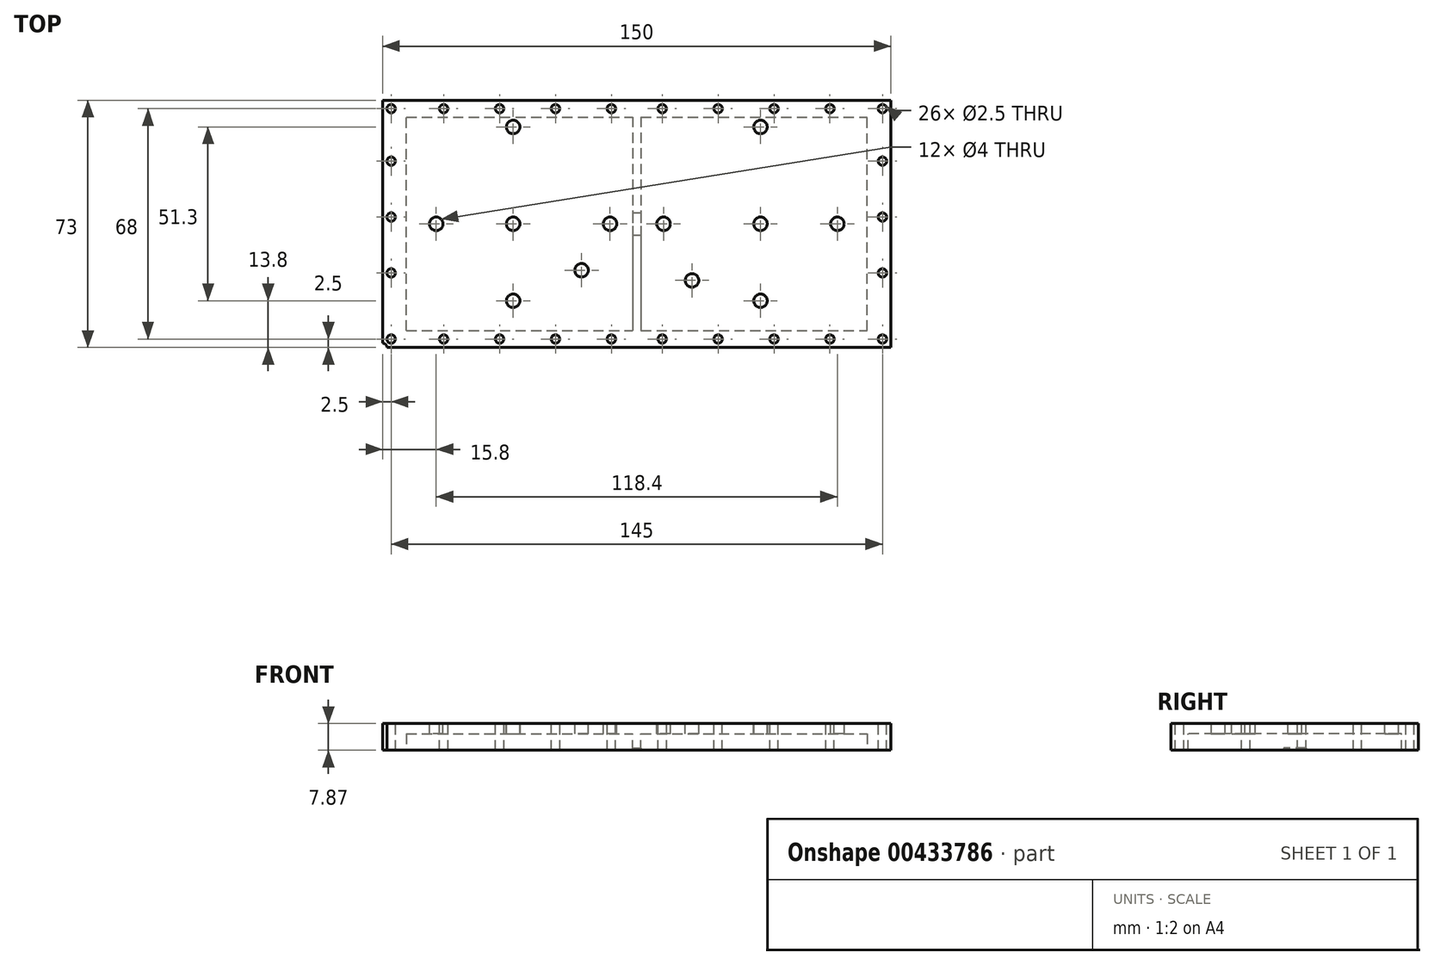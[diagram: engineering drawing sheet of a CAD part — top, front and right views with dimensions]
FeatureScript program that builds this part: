
annotation { "Feature Type Name" : "Feature", "Feature Type Description" : "" }
export const myFeature = defineFeature(function(context is Context, id is Id, definition is map)
    precondition{}
    {
        {
            var Q0;
            Q0=qCreatedBy(makeId("Top.planeOp"),FACE);
            var sketch = newSketch(context, id + "F0", { "sketchPlane" : qUnion([Q0])});
            skLineSegment(sketch, "E0.bottom", {"start": v(0, 0) * mm, "end": v(150, 0) * mm});
            skLineSegment(sketch, "E0.top", {"start": v(0, 73) * mm, "end": v(150, 73) * mm});
            skLineSegment(sketch, "E0.left", {"start": v(0, 0) * mm, "end": v(0, 73) * mm});
            skLineSegment(sketch, "E0.right", {"start": v(150, 0) * mm, "end": v(150, 73) * mm});
            skSolve(sketch);
        }
        {
            var Q0;
            Q0=qSketchRegion(id+"F0",true);
            extrude(context, id + "F1", {"entities" : qUnion([Q0]), "depth" : 7.87 * mm});
        }
        {
            var Q0;
            Q0=qCreatedBy(makeId("Top.planeOp"),FACE);
            var sketch = newSketch(context, id + "F2", { "sketchPlane" : qUnion([Q0])});
            skLineSegment(sketch, "E1.bottom", {"start": v(7, 5) * mm, "end": v(143, 5) * mm});
            skLineSegment(sketch, "E1.top", {"start": v(7, 68) * mm, "end": v(143, 68) * mm});
            skLineSegment(sketch, "E1.left", {"start": v(7, 5) * mm, "end": v(7, 68) * mm});
            skLineSegment(sketch, "E1.right", {"start": v(143, 5) * mm, "end": v(143, 68) * mm});
            skSolve(sketch);
        }
        {
            var Q0;
            Q0=qSketchRegion(id+"F2",true);
            extrude(context, id + "F3", {"entities" : qUnion([Q0]), "operationType" : NewBodyOperationType.REMOVE, "depth" : 4.87 * mm});
        }
        {
            var Q0;
            Q0=makeQuery(id+"F1.opExtrude","CAP_FACE",FACE,{"disambiguationData":[OSD([sQuery(id+"F0.wireOp",EDGE,"E0.bottom"),sQuery(id+"F0.wireOp",EDGE,"E0.top"),sQuery(id+"F0.wireOp",EDGE,"E0.left"),sQuery(id+"F0.wireOp",EDGE,"E0.right")])],"isStart":false});
            var sketch = newSketch(context, id + "F4", { "sketchPlane" : qUnion([Q0])});
            skCircle(sketch, "E2", {"center": v(2.5, 2.5) * mm, "radius": 1.25 * mm});
            skSolve(sketch);
        }
        {
            var Q0;
            Q0=qSketchRegion(id+"F4",true);
            extrude(context, id + "F5", {"entities" : qUnion([Q0]), "operationType" : NewBodyOperationType.REMOVE, "oppositeDirection" : true, "depth" : 7.87 * mm});
        }
        {
            var Q0;
            Q0=makeQuery(id+"F1.opExtrude","CAP_FACE",FACE,{"disambiguationData":[OSD([sQuery(id+"F0.wireOp",EDGE,"E0.bottom"),sQuery(id+"F0.wireOp",EDGE,"E0.top"),sQuery(id+"F0.wireOp",EDGE,"E0.left"),sQuery(id+"F0.wireOp",EDGE,"E0.right")])],"isStart":false});
            var sketch = newSketch(context, id + "F6", { "sketchPlane" : qUnion([Q0])});
            skCircle(sketch, "E3", {"center": v(18, 2.5) * mm, "radius": 1.25 * mm});
            skSolve(sketch);
        }
        {
            var Q0;
            Q0=qSketchRegion(id+"F6",true);
            extrude(context, id + "F7", {"entities" : qUnion([Q0]), "operationType" : NewBodyOperationType.REMOVE, "oppositeDirection" : true, "depth" : 7.87 * mm});
        }
        {
            var Q0;
            Q0=makeQuery(id+"F1.opExtrude","CAP_FACE",FACE,{"disambiguationData":[OSD([sQuery(id+"F0.wireOp",EDGE,"E0.bottom"),sQuery(id+"F0.wireOp",EDGE,"E0.top"),sQuery(id+"F0.wireOp",EDGE,"E0.left"),sQuery(id+"F0.wireOp",EDGE,"E0.right")])],"isStart":false});
            var sketch = newSketch(context, id + "F8", { "sketchPlane" : qUnion([Q0])});
            skCircle(sketch, "E4", {"center": v(34.5, 2.5) * mm, "radius": 1.25 * mm});
            skSolve(sketch);
        }
        {
            var Q0;
            Q0=qSketchRegion(id+"F8",true);
            extrude(context, id + "F9", {"entities" : qUnion([Q0]), "operationType" : NewBodyOperationType.REMOVE, "oppositeDirection" : true, "depth" : 7.87 * mm});
        }
        {
            var Q0;
            Q0=makeQuery(id+"F1.opExtrude","CAP_FACE",FACE,{"disambiguationData":[OSD([sQuery(id+"F0.wireOp",EDGE,"E0.bottom"),sQuery(id+"F0.wireOp",EDGE,"E0.top"),sQuery(id+"F0.wireOp",EDGE,"E0.left"),sQuery(id+"F0.wireOp",EDGE,"E0.right")])],"isStart":false});
            var sketch = newSketch(context, id + "F10", { "sketchPlane" : qUnion([Q0])});
            skCircle(sketch, "E5", {"center": v(51, 2.5) * mm, "radius": 1.25 * mm});
            skSolve(sketch);
        }
        {
            var Q0;
            Q0=qSketchRegion(id+"F10",true);
            extrude(context, id + "F11", {"entities" : qUnion([Q0]), "operationType" : NewBodyOperationType.REMOVE, "oppositeDirection" : true, "depth" : 7.87 * mm});
        }
        {
            var Q0;
            Q0=makeQuery(id+"F1.opExtrude","CAP_FACE",FACE,{"disambiguationData":[OSD([sQuery(id+"F0.wireOp",EDGE,"E0.bottom"),sQuery(id+"F0.wireOp",EDGE,"E0.top"),sQuery(id+"F0.wireOp",EDGE,"E0.left"),sQuery(id+"F0.wireOp",EDGE,"E0.right")])],"isStart":false});
            var sketch = newSketch(context, id + "F12", { "sketchPlane" : qUnion([Q0])});
            skCircle(sketch, "E6", {"center": v(67.5, 2.5) * mm, "radius": 1.25 * mm});
            skSolve(sketch);
        }
        {
            var Q0;
            Q0=qSketchRegion(id+"F12",true);
            extrude(context, id + "F13", {"entities" : qUnion([Q0]), "operationType" : NewBodyOperationType.REMOVE, "oppositeDirection" : true, "depth" : 7.87 * mm});
        }
        {
            var Q0;
            Q0=makeQuery(id+"F1.opExtrude","CAP_FACE",FACE,{"disambiguationData":[OSD([sQuery(id+"F0.wireOp",EDGE,"E0.bottom"),sQuery(id+"F0.wireOp",EDGE,"E0.top"),sQuery(id+"F0.wireOp",EDGE,"E0.left"),sQuery(id+"F0.wireOp",EDGE,"E0.right")])],"isStart":false});
            var sketch = newSketch(context, id + "F14", { "sketchPlane" : qUnion([Q0])});
            skCircle(sketch, "E7", {"center": v(82.5, 2.5) * mm, "radius": 1.25 * mm});
            skSolve(sketch);
        }
        {
            var Q0;
            Q0=qSketchRegion(id+"F14",true);
            extrude(context, id + "F15", {"entities" : qUnion([Q0]), "operationType" : NewBodyOperationType.REMOVE, "oppositeDirection" : true, "depth" : 7.87 * mm});
        }
        {
            var Q0;
            Q0=makeQuery(id+"F1.opExtrude","CAP_FACE",FACE,{"disambiguationData":[OSD([sQuery(id+"F0.wireOp",EDGE,"E0.bottom"),sQuery(id+"F0.wireOp",EDGE,"E0.top"),sQuery(id+"F0.wireOp",EDGE,"E0.left"),sQuery(id+"F0.wireOp",EDGE,"E0.right")])],"isStart":false});
            var sketch = newSketch(context, id + "F16", { "sketchPlane" : qUnion([Q0])});
            skCircle(sketch, "E8", {"center": v(99, 2.5) * mm, "radius": 1.25 * mm});
            skSolve(sketch);
        }
        {
            var Q0;
            Q0=qSketchRegion(id+"F16",true);
            extrude(context, id + "F17", {"entities" : qUnion([Q0]), "operationType" : NewBodyOperationType.REMOVE, "oppositeDirection" : true, "depth" : 7.87 * mm});
        }
        {
            var Q0;
            Q0=makeQuery(id+"F1.opExtrude","CAP_FACE",FACE,{"disambiguationData":[OSD([sQuery(id+"F0.wireOp",EDGE,"E0.bottom"),sQuery(id+"F0.wireOp",EDGE,"E0.top"),sQuery(id+"F0.wireOp",EDGE,"E0.left"),sQuery(id+"F0.wireOp",EDGE,"E0.right")])],"isStart":false});
            var sketch = newSketch(context, id + "F18", { "sketchPlane" : qUnion([Q0])});
            skCircle(sketch, "E9", {"center": v(115.5, 2.5) * mm, "radius": 1.25 * mm});
            skSolve(sketch);
        }
        {
            var Q0;
            Q0=qSketchRegion(id+"F18",true);
            extrude(context, id + "F19", {"entities" : qUnion([Q0]), "operationType" : NewBodyOperationType.REMOVE, "oppositeDirection" : true, "depth" : 7.87 * mm});
        }
        {
            var Q0;
            Q0=makeQuery(id+"F1.opExtrude","CAP_FACE",FACE,{"disambiguationData":[OSD([sQuery(id+"F0.wireOp",EDGE,"E0.bottom"),sQuery(id+"F0.wireOp",EDGE,"E0.top"),sQuery(id+"F0.wireOp",EDGE,"E0.left"),sQuery(id+"F0.wireOp",EDGE,"E0.right")])],"isStart":false});
            var sketch = newSketch(context, id + "F20", { "sketchPlane" : qUnion([Q0])});
            skCircle(sketch, "E10", {"center": v(132, 2.5) * mm, "radius": 1.25 * mm});
            skSolve(sketch);
        }
        {
            var Q0;
            Q0=qSketchRegion(id+"F20",true);
            extrude(context, id + "F21", {"entities" : qUnion([Q0]), "operationType" : NewBodyOperationType.REMOVE, "oppositeDirection" : true, "depth" : 7.87 * mm});
        }
        {
            var Q0;
            Q0=makeQuery(id+"F1.opExtrude","CAP_FACE",FACE,{"disambiguationData":[OSD([sQuery(id+"F0.wireOp",EDGE,"E0.bottom"),sQuery(id+"F0.wireOp",EDGE,"E0.top"),sQuery(id+"F0.wireOp",EDGE,"E0.left"),sQuery(id+"F0.wireOp",EDGE,"E0.right")])],"isStart":false});
            var sketch = newSketch(context, id + "F22", { "sketchPlane" : qUnion([Q0])});
            skCircle(sketch, "E11", {"center": v(147.5, 2.5) * mm, "radius": 1.25 * mm});
            skSolve(sketch);
        }
        {
            var Q0;
            Q0=qSketchRegion(id+"F22",true);
            extrude(context, id + "F23", {"entities" : qUnion([Q0]), "operationType" : NewBodyOperationType.REMOVE, "oppositeDirection" : true, "depth" : 7.87 * mm});
        }
        {
            var Q0;
            Q0=makeQuery(id+"F1.opExtrude","CAP_FACE",FACE,{"disambiguationData":[OSD([sQuery(id+"F0.wireOp",EDGE,"E0.bottom"),sQuery(id+"F0.wireOp",EDGE,"E0.top"),sQuery(id+"F0.wireOp",EDGE,"E0.left"),sQuery(id+"F0.wireOp",EDGE,"E0.right")])],"isStart":false});
            var sketch = newSketch(context, id + "F24", { "sketchPlane" : qUnion([Q0])});
            skCircle(sketch, "E12", {"center": v(2.5, 22) * mm, "radius": 1.25 * mm});
            skSolve(sketch);
        }
        {
            var Q0;
            Q0=qSketchRegion(id+"F24",true);
            extrude(context, id + "F25", {"entities" : qUnion([Q0]), "operationType" : NewBodyOperationType.REMOVE, "oppositeDirection" : true, "depth" : 7.87 * mm});
        }
        {
            var Q0;
            Q0=makeQuery(id+"F1.opExtrude","CAP_FACE",FACE,{"disambiguationData":[OSD([sQuery(id+"F0.wireOp",EDGE,"E0.bottom"),sQuery(id+"F0.wireOp",EDGE,"E0.top"),sQuery(id+"F0.wireOp",EDGE,"E0.left"),sQuery(id+"F0.wireOp",EDGE,"E0.right")])],"isStart":false});
            var sketch = newSketch(context, id + "F26", { "sketchPlane" : qUnion([Q0])});
            skCircle(sketch, "E13", {"center": v(147.5, 22) * mm, "radius": 1.25 * mm});
            skSolve(sketch);
        }
        {
            var Q0;
            Q0=qSketchRegion(id+"F26",true);
            extrude(context, id + "F27", {"entities" : qUnion([Q0]), "operationType" : NewBodyOperationType.REMOVE, "oppositeDirection" : true, "depth" : 7.87 * mm});
        }
        {
            var Q0;
            Q0=makeQuery(id+"F1.opExtrude","CAP_FACE",FACE,{"disambiguationData":[OSD([sQuery(id+"F0.wireOp",EDGE,"E0.bottom"),sQuery(id+"F0.wireOp",EDGE,"E0.top"),sQuery(id+"F0.wireOp",EDGE,"E0.left"),sQuery(id+"F0.wireOp",EDGE,"E0.right")])],"isStart":false});
            var sketch = newSketch(context, id + "F28", { "sketchPlane" : qUnion([Q0])});
            skCircle(sketch, "E14", {"center": v(147.5, 38.5) * mm, "radius": 1.25 * mm});
            skSolve(sketch);
        }
        {
            var Q0;
            Q0=qSketchRegion(id+"F28",true);
            extrude(context, id + "F29", {"entities" : qUnion([Q0]), "operationType" : NewBodyOperationType.REMOVE, "oppositeDirection" : true, "depth" : 7.87 * mm});
        }
        {
            var Q0;
            Q0=makeQuery(id+"F1.opExtrude","CAP_FACE",FACE,{"disambiguationData":[OSD([sQuery(id+"F0.wireOp",EDGE,"E0.bottom"),sQuery(id+"F0.wireOp",EDGE,"E0.top"),sQuery(id+"F0.wireOp",EDGE,"E0.left"),sQuery(id+"F0.wireOp",EDGE,"E0.right")])],"isStart":false});
            var sketch = newSketch(context, id + "F30", { "sketchPlane" : qUnion([Q0])});
            skCircle(sketch, "E15", {"center": v(2.5, 38.5) * mm, "radius": 1.25 * mm});
            skSolve(sketch);
        }
        {
            var Q0;
            Q0=qSketchRegion(id+"F30",true);
            extrude(context, id + "F31", {"entities" : qUnion([Q0]), "operationType" : NewBodyOperationType.REMOVE, "oppositeDirection" : true, "depth" : 7.87 * mm});
        }
        {
            var Q0;
            Q0=makeQuery(id+"F1.opExtrude","CAP_FACE",FACE,{"disambiguationData":[OSD([sQuery(id+"F0.wireOp",EDGE,"E0.bottom"),sQuery(id+"F0.wireOp",EDGE,"E0.top"),sQuery(id+"F0.wireOp",EDGE,"E0.left"),sQuery(id+"F0.wireOp",EDGE,"E0.right")])],"isStart":false});
            var sketch = newSketch(context, id + "F32", { "sketchPlane" : qUnion([Q0])});
            skCircle(sketch, "E16", {"center": v(2.5, 55) * mm, "radius": 1.25 * mm});
            skSolve(sketch);
        }
        {
            var Q0;
            Q0=qSketchRegion(id+"F32",true);
            extrude(context, id + "F33", {"entities" : qUnion([Q0]), "operationType" : NewBodyOperationType.REMOVE, "oppositeDirection" : true, "depth" : 7.87 * mm});
        }
        {
            var Q0;
            Q0=makeQuery(id+"F1.opExtrude","CAP_FACE",FACE,{"disambiguationData":[OSD([sQuery(id+"F0.wireOp",EDGE,"E0.bottom"),sQuery(id+"F0.wireOp",EDGE,"E0.top"),sQuery(id+"F0.wireOp",EDGE,"E0.left"),sQuery(id+"F0.wireOp",EDGE,"E0.right")])],"isStart":false});
            var sketch = newSketch(context, id + "F34", { "sketchPlane" : qUnion([Q0])});
            skCircle(sketch, "E17", {"center": v(147.5, 55) * mm, "radius": 1.25 * mm});
            skSolve(sketch);
        }
        {
            var Q0;
            Q0=qSketchRegion(id+"F34",true);
            extrude(context, id + "F35", {"entities" : qUnion([Q0]), "operationType" : NewBodyOperationType.REMOVE, "oppositeDirection" : true, "depth" : 7.87 * mm});
        }
        {
            var Q0;
            Q0=makeQuery(id+"F1.opExtrude","CAP_FACE",FACE,{"disambiguationData":[OSD([sQuery(id+"F0.wireOp",EDGE,"E0.bottom"),sQuery(id+"F0.wireOp",EDGE,"E0.top"),sQuery(id+"F0.wireOp",EDGE,"E0.left"),sQuery(id+"F0.wireOp",EDGE,"E0.right")])],"isStart":false});
            var sketch = newSketch(context, id + "F36", { "sketchPlane" : qUnion([Q0])});
            skCircle(sketch, "E18", {"center": v(2.5, 70.5) * mm, "radius": 1.25 * mm});
            skSolve(sketch);
        }
        {
            var Q0;
            Q0=qSketchRegion(id+"F36",true);
            extrude(context, id + "F37", {"entities" : qUnion([Q0]), "operationType" : NewBodyOperationType.REMOVE, "oppositeDirection" : true, "depth" : 7.87 * mm});
        }
        {
            var Q0;
            Q0=makeQuery(id+"F1.opExtrude","CAP_FACE",FACE,{"disambiguationData":[OSD([sQuery(id+"F0.wireOp",EDGE,"E0.bottom"),sQuery(id+"F0.wireOp",EDGE,"E0.top"),sQuery(id+"F0.wireOp",EDGE,"E0.left"),sQuery(id+"F0.wireOp",EDGE,"E0.right")])],"isStart":false});
            var sketch = newSketch(context, id + "F38", { "sketchPlane" : qUnion([Q0])});
            skCircle(sketch, "E19", {"center": v(147.5, 70.5) * mm, "radius": 1.25 * mm});
            skSolve(sketch);
        }
        {
            var Q0;
            Q0=qSketchRegion(id+"F38",true);
            extrude(context, id + "F39", {"entities" : qUnion([Q0]), "operationType" : NewBodyOperationType.REMOVE, "oppositeDirection" : true, "depth" : 7.87 * mm});
        }
        {
            var Q0;
            Q0=makeQuery(id+"F1.opExtrude","CAP_FACE",FACE,{"disambiguationData":[OSD([sQuery(id+"F0.wireOp",EDGE,"E0.bottom"),sQuery(id+"F0.wireOp",EDGE,"E0.top"),sQuery(id+"F0.wireOp",EDGE,"E0.left"),sQuery(id+"F0.wireOp",EDGE,"E0.right")])],"isStart":false});
            var sketch = newSketch(context, id + "F40", { "sketchPlane" : qUnion([Q0])});
            skCircle(sketch, "E20", {"center": v(18, 70.5) * mm, "radius": 1.25 * mm});
            skSolve(sketch);
        }
        {
            var Q0;
            Q0=qSketchRegion(id+"F40",true);
            extrude(context, id + "F41", {"entities" : qUnion([Q0]), "operationType" : NewBodyOperationType.REMOVE, "oppositeDirection" : true, "depth" : 7.87 * mm});
        }
        {
            var Q0;
            Q0=makeQuery(id+"F1.opExtrude","CAP_FACE",FACE,{"disambiguationData":[OSD([sQuery(id+"F0.wireOp",EDGE,"E0.bottom"),sQuery(id+"F0.wireOp",EDGE,"E0.top"),sQuery(id+"F0.wireOp",EDGE,"E0.left"),sQuery(id+"F0.wireOp",EDGE,"E0.right")])],"isStart":false});
            var sketch = newSketch(context, id + "F42", { "sketchPlane" : qUnion([Q0])});
            skCircle(sketch, "E21", {"center": v(132, 70.5) * mm, "radius": 1.25 * mm});
            skSolve(sketch);
        }
        {
            var Q0;
            Q0=qSketchRegion(id+"F42",true);
            extrude(context, id + "F43", {"entities" : qUnion([Q0]), "operationType" : NewBodyOperationType.REMOVE, "oppositeDirection" : true, "depth" : 7.87 * mm});
        }
        {
            var Q0;
            Q0=makeQuery(id+"F1.opExtrude","CAP_FACE",FACE,{"disambiguationData":[OSD([sQuery(id+"F0.wireOp",EDGE,"E0.bottom"),sQuery(id+"F0.wireOp",EDGE,"E0.top"),sQuery(id+"F0.wireOp",EDGE,"E0.left"),sQuery(id+"F0.wireOp",EDGE,"E0.right")])],"isStart":false});
            var sketch = newSketch(context, id + "F44", { "sketchPlane" : qUnion([Q0])});
            skCircle(sketch, "E22", {"center": v(34.5, 70.5) * mm, "radius": 1.25 * mm});
            skCircle(sketch, "E23", {"center": v(0, 0) * mm, "radius": 1.25 * mm});
            skSolve(sketch);
        }
        {
            var Q0;
            Q0=qSketchRegion(id+"F44",true);
            extrude(context, id + "F45", {"entities" : qUnion([Q0]), "operationType" : NewBodyOperationType.REMOVE, "oppositeDirection" : true, "depth" : 7.87 * mm});
        }
        {
            var Q0;
            Q0=makeQuery(id+"F1.opExtrude","CAP_FACE",FACE,{"disambiguationData":[OSD([sQuery(id+"F0.wireOp",EDGE,"E0.bottom"),sQuery(id+"F0.wireOp",EDGE,"E0.top"),sQuery(id+"F0.wireOp",EDGE,"E0.left"),sQuery(id+"F0.wireOp",EDGE,"E0.right")])],"isStart":false});
            var sketch = newSketch(context, id + "F46", { "sketchPlane" : qUnion([Q0])});
            skCircle(sketch, "E24", {"center": v(115.5, 70.5) * mm, "radius": 1.25 * mm});
            skSolve(sketch);
        }
        {
            var Q0;
            Q0=qSketchRegion(id+"F46",true);
            extrude(context, id + "F47", {"entities" : qUnion([Q0]), "operationType" : NewBodyOperationType.REMOVE, "oppositeDirection" : true, "depth" : 7.87 * mm});
        }
        {
            var Q0;
            Q0=makeQuery(id+"F1.opExtrude","CAP_FACE",FACE,{"disambiguationData":[OSD([sQuery(id+"F0.wireOp",EDGE,"E0.bottom"),sQuery(id+"F0.wireOp",EDGE,"E0.top"),sQuery(id+"F0.wireOp",EDGE,"E0.left"),sQuery(id+"F0.wireOp",EDGE,"E0.right")])],"isStart":false});
            var sketch = newSketch(context, id + "F48", { "sketchPlane" : qUnion([Q0])});
            skCircle(sketch, "E25", {"center": v(51, 70.5) * mm, "radius": 1.25 * mm});
            skSolve(sketch);
        }
        {
            var Q0;
            Q0=qSketchRegion(id+"F48",true);
            extrude(context, id + "F49", {"entities" : qUnion([Q0]), "operationType" : NewBodyOperationType.REMOVE, "oppositeDirection" : true, "depth" : 7.87 * mm});
        }
        {
            var Q0;
            Q0=makeQuery(id+"F1.opExtrude","CAP_FACE",FACE,{"disambiguationData":[OSD([sQuery(id+"F0.wireOp",EDGE,"E0.bottom"),sQuery(id+"F0.wireOp",EDGE,"E0.top"),sQuery(id+"F0.wireOp",EDGE,"E0.left"),sQuery(id+"F0.wireOp",EDGE,"E0.right")])],"isStart":false});
            var sketch = newSketch(context, id + "F50", { "sketchPlane" : qUnion([Q0])});
            skCircle(sketch, "E26", {"center": v(67.5, 70.5) * mm, "radius": 1.25 * mm});
            skSolve(sketch);
        }
        {
            var Q0;
            Q0=qSketchRegion(id+"F50",true);
            extrude(context, id + "F51", {"entities" : qUnion([Q0]), "operationType" : NewBodyOperationType.REMOVE, "oppositeDirection" : true, "depth" : 7.87 * mm});
        }
        {
            var Q0;
            Q0=makeQuery(id+"F1.opExtrude","CAP_FACE",FACE,{"disambiguationData":[OSD([sQuery(id+"F0.wireOp",EDGE,"E0.bottom"),sQuery(id+"F0.wireOp",EDGE,"E0.top"),sQuery(id+"F0.wireOp",EDGE,"E0.left"),sQuery(id+"F0.wireOp",EDGE,"E0.right")])],"isStart":false});
            var sketch = newSketch(context, id + "F52", { "sketchPlane" : qUnion([Q0])});
            skCircle(sketch, "E27", {"center": v(82.5, 70.5) * mm, "radius": 1.25 * mm});
            skSolve(sketch);
        }
        {
            var Q0;
            Q0=qSketchRegion(id+"F52",true);
            extrude(context, id + "F53", {"entities" : qUnion([Q0]), "operationType" : NewBodyOperationType.REMOVE, "oppositeDirection" : true, "depth" : 7.87 * mm});
        }
        {
            var Q0;
            Q0=makeQuery(id+"F1.opExtrude","CAP_FACE",FACE,{"disambiguationData":[OSD([sQuery(id+"F0.wireOp",EDGE,"E0.bottom"),sQuery(id+"F0.wireOp",EDGE,"E0.top"),sQuery(id+"F0.wireOp",EDGE,"E0.left"),sQuery(id+"F0.wireOp",EDGE,"E0.right")])],"isStart":false});
            var sketch = newSketch(context, id + "F54", { "sketchPlane" : qUnion([Q0])});
            skCircle(sketch, "E28", {"center": v(99, 70.5) * mm, "radius": 1.25 * mm});
            skSolve(sketch);
        }
        {
            var Q0;
            Q0=qSketchRegion(id+"F54",true);
            extrude(context, id + "F55", {"entities" : qUnion([Q0]), "operationType" : NewBodyOperationType.REMOVE, "oppositeDirection" : true, "depth" : 7.87 * mm});
        }
        {
            var Q0;
            Q0=makeQuery(id+"F1.opExtrude","CAP_FACE",FACE,{"disambiguationData":[OSD([sQuery(id+"F0.wireOp",EDGE,"E0.bottom"),sQuery(id+"F0.wireOp",EDGE,"E0.top"),sQuery(id+"F0.wireOp",EDGE,"E0.left"),sQuery(id+"F0.wireOp",EDGE,"E0.right")])],"isStart":false});
            var sketch = newSketch(context, id + "F56", { "sketchPlane" : qUnion([Q0])});
            skCircle(sketch, "E29", {"center": v(38.5, 65.1) * mm, "radius": 2 * mm});
            skSolve(sketch);
        }
        {
            var Q0;
            Q0=qSketchRegion(id+"F56",true);
            extrude(context, id + "F57", {"entities" : qUnion([Q0]), "operationType" : NewBodyOperationType.REMOVE, "oppositeDirection" : true, "depth" : 3 * mm});
        }
        {
            var Q0;
            Q0=makeQuery(id+"F1.opExtrude","CAP_FACE",FACE,{"disambiguationData":[OSD([sQuery(id+"F0.wireOp",EDGE,"E0.bottom"),sQuery(id+"F0.wireOp",EDGE,"E0.top"),sQuery(id+"F0.wireOp",EDGE,"E0.left"),sQuery(id+"F0.wireOp",EDGE,"E0.right")])],"isStart":false});
            var sketch = newSketch(context, id + "F58", { "sketchPlane" : qUnion([Q0])});
            skCircle(sketch, "E30", {"center": v(15.8, 36.5) * mm, "radius": 2 * mm});
            skSolve(sketch);
        }
        {
            var Q0;
            Q0=qSketchRegion(id+"F58",true);
            extrude(context, id + "F59", {"entities" : qUnion([Q0]), "operationType" : NewBodyOperationType.REMOVE, "oppositeDirection" : true, "depth" : 3 * mm});
        }
        {
            var Q0;
            Q0=makeQuery(id+"F1.opExtrude","CAP_FACE",FACE,{"disambiguationData":[OSD([sQuery(id+"F0.wireOp",EDGE,"E0.bottom"),sQuery(id+"F0.wireOp",EDGE,"E0.top"),sQuery(id+"F0.wireOp",EDGE,"E0.left"),sQuery(id+"F0.wireOp",EDGE,"E0.right")])],"isStart":false});
            var sketch = newSketch(context, id + "F60", { "sketchPlane" : qUnion([Q0])});
            skCircle(sketch, "E31", {"center": v(67.1, 36.5) * mm, "radius": 2 * mm});
            skSolve(sketch);
        }
        {
            var Q0;
            Q0=qSketchRegion(id+"F60",true);
            extrude(context, id + "F61", {"entities" : qUnion([Q0]), "operationType" : NewBodyOperationType.REMOVE, "oppositeDirection" : true, "depth" : 3 * mm});
        }
        {
            var Q0;
            Q0=makeQuery(id+"F1.opExtrude","CAP_FACE",FACE,{"disambiguationData":[OSD([sQuery(id+"F0.wireOp",EDGE,"E0.bottom"),sQuery(id+"F0.wireOp",EDGE,"E0.top"),sQuery(id+"F0.wireOp",EDGE,"E0.left"),sQuery(id+"F0.wireOp",EDGE,"E0.right")])],"isStart":false});
            var sketch = newSketch(context, id + "F62", { "sketchPlane" : qUnion([Q0])});
            skCircle(sketch, "E32", {"center": v(111.5, 65.1) * mm, "radius": 2 * mm});
            skSolve(sketch);
        }
        {
            var Q0;
            Q0=qSketchRegion(id+"F62",true);
            extrude(context, id + "F63", {"entities" : qUnion([Q0]), "operationType" : NewBodyOperationType.REMOVE, "oppositeDirection" : true, "depth" : 3 * mm});
        }
        {
            var Q0;
            Q0=makeQuery(id+"F1.opExtrude","CAP_FACE",FACE,{"disambiguationData":[OSD([sQuery(id+"F0.wireOp",EDGE,"E0.bottom"),sQuery(id+"F0.wireOp",EDGE,"E0.top"),sQuery(id+"F0.wireOp",EDGE,"E0.left"),sQuery(id+"F0.wireOp",EDGE,"E0.right")])],"isStart":false});
            var sketch = newSketch(context, id + "F64", { "sketchPlane" : qUnion([Q0])});
            skCircle(sketch, "E33", {"center": v(82.9, 36.5) * mm, "radius": 2 * mm});
            skSolve(sketch);
        }
        {
            var Q0;
            Q0=qSketchRegion(id+"F64",true);
            extrude(context, id + "F65", {"entities" : qUnion([Q0]), "operationType" : NewBodyOperationType.REMOVE, "oppositeDirection" : true, "depth" : 3 * mm});
        }
        {
            var Q0;
            Q0=makeQuery(id+"F1.opExtrude","CAP_FACE",FACE,{"disambiguationData":[OSD([sQuery(id+"F0.wireOp",EDGE,"E0.bottom"),sQuery(id+"F0.wireOp",EDGE,"E0.top"),sQuery(id+"F0.wireOp",EDGE,"E0.left"),sQuery(id+"F0.wireOp",EDGE,"E0.right")])],"isStart":false});
            var sketch = newSketch(context, id + "F66", { "sketchPlane" : qUnion([Q0])});
            skCircle(sketch, "E34", {"center": v(134.2, 36.5) * mm, "radius": 2 * mm});
            skSolve(sketch);
        }
        {
            var Q0;
            Q0=qSketchRegion(id+"F66",true);
            extrude(context, id + "F67", {"entities" : qUnion([Q0]), "operationType" : NewBodyOperationType.REMOVE, "oppositeDirection" : true, "depth" : 3 * mm});
        }
        {
            var Q0;
            Q0=makeQuery(id+"F1.opExtrude","CAP_FACE",FACE,{"disambiguationData":[OSD([sQuery(id+"F0.wireOp",EDGE,"E0.bottom"),sQuery(id+"F0.wireOp",EDGE,"E0.top"),sQuery(id+"F0.wireOp",EDGE,"E0.left"),sQuery(id+"F0.wireOp",EDGE,"E0.right")])],"isStart":false});
            var sketch = newSketch(context, id + "F68", { "sketchPlane" : qUnion([Q0])});
            skCircle(sketch, "E35", {"center": v(58.7, 22.8) * mm, "radius": 2 * mm});
            skSolve(sketch);
        }
        {
            var Q0;
            Q0=qSketchRegion(id+"F68",true);
            extrude(context, id + "F69", {"entities" : qUnion([Q0]), "operationType" : NewBodyOperationType.REMOVE, "oppositeDirection" : true, "depth" : 3 * mm});
        }
        {
            var Q0;
            Q0=makeQuery(id+"F1.opExtrude","CAP_FACE",FACE,{"disambiguationData":[OSD([sQuery(id+"F0.wireOp",EDGE,"E0.bottom"),sQuery(id+"F0.wireOp",EDGE,"E0.top"),sQuery(id+"F0.wireOp",EDGE,"E0.left"),sQuery(id+"F0.wireOp",EDGE,"E0.right")])],"isStart":false});
            var sketch = newSketch(context, id + "F70", { "sketchPlane" : qUnion([Q0])});
            skCircle(sketch, "E36", {"center": v(91.3, 19.8) * mm, "radius": 2 * mm});
            skSolve(sketch);
        }
        {
            var Q0;
            Q0=qSketchRegion(id+"F70",true);
            extrude(context, id + "F71", {"entities" : qUnion([Q0]), "operationType" : NewBodyOperationType.REMOVE, "oppositeDirection" : true, "depth" : 3 * mm});
        }
        {
            var Q0;
            Q0=makeQuery(id+"F3.boolean.opBoolean","COPY",FACE,{"derivedFrom":makeQuery(id+"F3.opExtrude","SWEPT_FACE",FACE,{"disambiguationData":[OSD([sQuery(id+"F2.wireOp",EDGE,"E1.bottom")])]})});
            var sketch = newSketch(context, id + "F72", { "sketchPlane" : qUnion([Q0])});
            skLineSegment(sketch, "E37.bottom", {"start": v(-73.75, 0) * mm, "end": v(-76.25, 0) * mm});
            skLineSegment(sketch, "E37.top", {"start": v(-73.75, 4.87) * mm, "end": v(-76.25, 4.87) * mm});
            skLineSegment(sketch, "E37.left", {"start": v(-73.75, 0) * mm, "end": v(-73.75, 4.87) * mm});
            skLineSegment(sketch, "E37.right", {"start": v(-76.25, 0) * mm, "end": v(-76.25, 4.87) * mm});
            skSolve(sketch);
        }
        {
            var Q0;
            Q0=makeQuery(id+"F72.imprint","IMPRINT",FACE,{"disambiguationData":[TD([[makeQuery(id+"F72.imprint","IMPRINT",EDGE,{"derivedFrom":sQuery(id+"F72.wireOp",EDGE,"E37.bottom")}),-1.0]])]});
            extrude(context, id + "F73", {"entities" : qUnion([Q0]), "operationType" : NewBodyOperationType.ADD, "depth" : 63 * mm});
        }
        {
            var Q0;
            Q0=makeQuery(id+"F73.boolean.opBoolean","MERGE",FACE,{"derivedFrom":[makeQuery(id+"F1.opExtrude","CAP_FACE",FACE,{"disambiguationData":[OSD([sQuery(id+"F0.wireOp",EDGE,"E0.bottom"),sQuery(id+"F0.wireOp",EDGE,"E0.top"),sQuery(id+"F0.wireOp",EDGE,"E0.left"),sQuery(id+"F0.wireOp",EDGE,"E0.right")])],"isStart":true}),makeQuery(id+"F73.opExtrude","SWEPT_FACE",FACE,{"disambiguationData":[OSD([sQuery(id+"F72.wireOp",EDGE,"E37.bottom")])]})]});
            var sketch = newSketch(context, id + "F74", { "sketchPlane" : qUnion([Q0])});
            skLineSegment(sketch, "E38.bottom", {"start": v(73.75, -33.25) * mm, "end": v(76.25, -33.25) * mm});
            skLineSegment(sketch, "E38.top", {"start": v(73.75, -39.75) * mm, "end": v(76.25, -39.75) * mm});
            skLineSegment(sketch, "E38.left", {"start": v(73.75, -33.25) * mm, "end": v(73.75, -39.75) * mm});
            skLineSegment(sketch, "E38.right", {"start": v(76.25, -33.25) * mm, "end": v(76.25, -39.75) * mm});
            skSolve(sketch);
        }
        {
            var Q0;
            Q0=qSketchRegion(id+"F74",true);
            extrude(context, id + "F75", {"entities" : qUnion([Q0]), "operationType" : NewBodyOperationType.REMOVE, "oppositeDirection" : true, "depth" : 0.62 * mm});
        }
        {
            var Q0;
            {var subQ0=sQuery(id+"F2.wireOp",EDGE,"E1.top");var subQ1=sQuery(id+"F2.wireOp",EDGE,"E1.bottom");var subQ2=sQuery(id+"F2.wireOp",EDGE,"E1.left");Q0=makeQuery(id+"F73.boolean.opBoolean","SPLIT",FACE,{"disambiguationData":[TD([makeQuery(id+"F3.boolean.opBoolean","COPY",FACE,{"derivedFrom":makeQuery(id+"F3.opExtrude","SWEPT_FACE",FACE,{"disambiguationData":[OSD([subQ2])]})})])],"derivedFrom":makeQuery(id+"F3.boolean.opBoolean","COPY",FACE,{"derivedFrom":makeQuery(id+"F3.opExtrude","CAP_FACE",FACE,{"disambiguationData":[OSD([subQ1,subQ0,subQ2,sQuery(id+"F2.wireOp",EDGE,"E1.right")])],"isStart":false})})});}
            var sketch = newSketch(context, id + "F76", { "sketchPlane" : qUnion([Q0])});
            skCircle(sketch, "E39", {"center": v(38.5, -13.8) * mm, "radius": 2 * mm});
            skSolve(sketch);
        }
        {
            var Q0;
            Q0=qSketchRegion(id+"F76",true);
            extrude(context, id + "F77", {"entities" : qUnion([Q0]), "operationType" : NewBodyOperationType.REMOVE, "oppositeDirection" : true, "depth" : 3 * mm});
        }
        {
            var Q0;
            {var subQ0=sQuery(id+"F2.wireOp",EDGE,"E1.left");var subQ1=sQuery(id+"F2.wireOp",EDGE,"E1.top");var subQ2=sQuery(id+"F2.wireOp",EDGE,"E1.bottom");Q0=makeQuery(id+"F73.boolean.opBoolean","SPLIT",FACE,{"disambiguationData":[TD([makeQuery(id+"F3.boolean.opBoolean","COPY",FACE,{"derivedFrom":makeQuery(id+"F3.opExtrude","SWEPT_FACE",FACE,{"disambiguationData":[OSD([subQ0])]})})])],"derivedFrom":makeQuery(id+"F3.boolean.opBoolean","COPY",FACE,{"derivedFrom":makeQuery(id+"F3.opExtrude","CAP_FACE",FACE,{"disambiguationData":[OSD([subQ2,subQ1,subQ0,sQuery(id+"F2.wireOp",EDGE,"E1.right")])],"isStart":false})})});}
            var sketch = newSketch(context, id + "F78", { "sketchPlane" : qUnion([Q0])});
            skCircle(sketch, "E40", {"center": v(38.5, -36.5) * mm, "radius": 2 * mm});
            skSolve(sketch);
        }
        {
            var Q0;
            {var subQ0=sQuery(id+"F2.wireOp",EDGE,"E1.right");var subQ1=sQuery(id+"F2.wireOp",EDGE,"E1.top");var subQ2=sQuery(id+"F2.wireOp",EDGE,"E1.bottom");Q0=makeQuery(id+"F73.boolean.opBoolean","SPLIT",FACE,{"disambiguationData":[TD([makeQuery(id+"F3.boolean.opBoolean","COPY",FACE,{"derivedFrom":makeQuery(id+"F3.opExtrude","SWEPT_FACE",FACE,{"disambiguationData":[OSD([subQ0])]})})])],"derivedFrom":makeQuery(id+"F3.boolean.opBoolean","COPY",FACE,{"derivedFrom":makeQuery(id+"F3.opExtrude","CAP_FACE",FACE,{"disambiguationData":[OSD([subQ2,subQ1,sQuery(id+"F2.wireOp",EDGE,"E1.left"),subQ0])],"isStart":false})})});}
            var sketch = newSketch(context, id + "F79", { "sketchPlane" : qUnion([Q0])});
            skCircle(sketch, "E41", {"center": v(111.5, -36.5) * mm, "radius": 2 * mm});
            skSolve(sketch);
        }
        {
            var Q0;
            Q0=qSketchRegion(id+"F79",true);
            extrude(context, id + "F80", {"entities" : qUnion([Q0]), "operationType" : NewBodyOperationType.REMOVE, "oppositeDirection" : true, "depth" : 3 * mm});
        }
        {
            var Q0;
            {var subQ0=sQuery(id+"F2.wireOp",EDGE,"E1.right");var subQ1=sQuery(id+"F2.wireOp",EDGE,"E1.top");var subQ2=sQuery(id+"F2.wireOp",EDGE,"E1.bottom");Q0=makeQuery(id+"F73.boolean.opBoolean","SPLIT",FACE,{"disambiguationData":[TD([makeQuery(id+"F3.boolean.opBoolean","COPY",FACE,{"derivedFrom":makeQuery(id+"F3.opExtrude","SWEPT_FACE",FACE,{"disambiguationData":[OSD([subQ0])]})})])],"derivedFrom":makeQuery(id+"F3.boolean.opBoolean","COPY",FACE,{"derivedFrom":makeQuery(id+"F3.opExtrude","CAP_FACE",FACE,{"disambiguationData":[OSD([subQ2,subQ1,sQuery(id+"F2.wireOp",EDGE,"E1.left"),subQ0])],"isStart":false})})});}
            var sketch = newSketch(context, id + "F81", { "sketchPlane" : qUnion([Q0])});
            skCircle(sketch, "E42", {"center": v(111.5, -13.8) * mm, "radius": 2 * mm});
            skSolve(sketch);
        }
        {
            var Q0;
            Q0=qSketchRegion(id+"F81",true);
            extrude(context, id + "F82", {"entities" : qUnion([Q0]), "operationType" : NewBodyOperationType.REMOVE, "oppositeDirection" : true, "depth" : 3 * mm});
        }
        {
            var Q0;
            Q0 = qSketchRegion(id + "F78", true);
            extrude(context, id + "F83", {"entities" : qUnion([Q0]), "operationType" : NewBodyOperationType.REMOVE, "oppositeDirection" : true, "depth" : 3 * mm});
        }
    });
